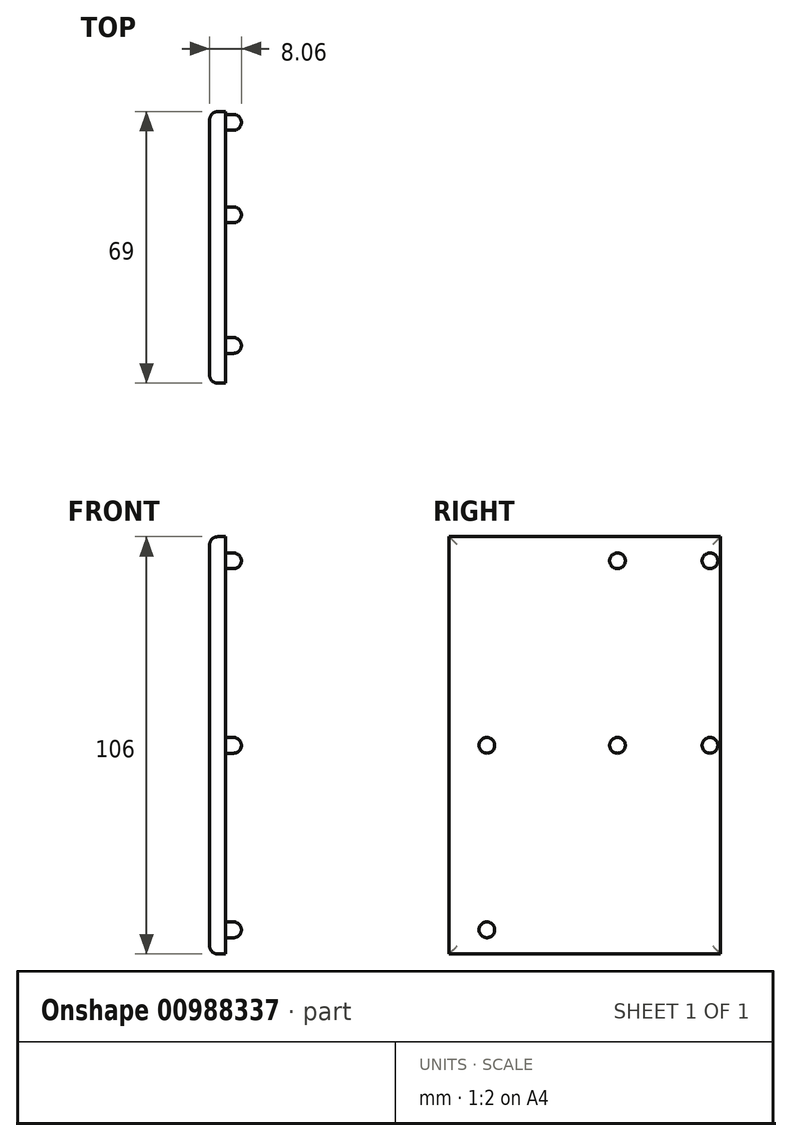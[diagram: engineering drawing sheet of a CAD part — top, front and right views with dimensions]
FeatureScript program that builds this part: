
annotation { "Feature Type Name" : "Feature", "Feature Type Description" : "" }
export const myFeature = defineFeature(function(context is Context, id is Id, definition is map)
    precondition{}
    {
        {
            var Q0;
            Q0=qCreatedBy(makeId("Front.planeOp"),FACE);
            var sketch = newSketch(context, id + "F0", { "sketchPlane" : qUnion([Q0])});
            skLineSegment(sketch, "E0.bottom", {"start": v(70.94, 60) * mm, "end": v(-59.06, 60) * mm});
            skLineSegment(sketch, "E0.top", {"start": v(70.94, -60) * mm, "end": v(-59.06, -60) * mm});
            skLineSegment(sketch, "E0.left", {"start": v(70.94, 60) * mm, "end": v(70.94, -60) * mm});
            skLineSegment(sketch, "E0.right", {"start": v(-59.06, 60) * mm, "end": v(-59.06, -60) * mm});
            skLineSegment(sketch, "E1.bottom", {"start": v(-59.06, 60) * mm, "end": v(70.94, 60) * mm});
            skLineSegment(sketch, "E1.top", {"start": v(-59.06, 53) * mm, "end": v(70.94, 53) * mm});
            skLineSegment(sketch, "E1.left", {"start": v(-59.06, 60) * mm, "end": v(-59.06, 53) * mm});
            skLineSegment(sketch, "E1.right", {"start": v(70.94, 60) * mm, "end": v(70.94, 53) * mm});
            skLineSegment(sketch, "E2.bottom", {"start": v(-59.06, -60) * mm, "end": v(70.94, -60) * mm});
            skLineSegment(sketch, "E2.top", {"start": v(-59.06, -53) * mm, "end": v(70.94, -53) * mm});
            skLineSegment(sketch, "E2.left", {"start": v(-59.06, -60) * mm, "end": v(-59.06, -53) * mm});
            skLineSegment(sketch, "E2.right", {"start": v(70.94, -60) * mm, "end": v(70.94, -53) * mm});
            skLineSegment(sketch, "E3.bottom", {"start": v(-59.06, 53) * mm, "end": v(-52.06, 53) * mm});
            skLineSegment(sketch, "E3.top", {"start": v(-59.06, -53) * mm, "end": v(-52.06, -53) * mm});
            skLineSegment(sketch, "E3.left", {"start": v(-59.06, 53) * mm, "end": v(-59.06, -53) * mm});
            skLineSegment(sketch, "E3.right", {"start": v(-52.06, 53) * mm, "end": v(-52.06, -53) * mm});
            skLineSegment(sketch, "E4.bottom", {"start": v(70.94, 53) * mm, "end": v(64.94, 53) * mm});
            skLineSegment(sketch, "E4.top", {"start": v(70.94, -53) * mm, "end": v(64.94, -53) * mm});
            skLineSegment(sketch, "E4.left", {"start": v(70.94, 53) * mm, "end": v(70.94, -53) * mm});
            skLineSegment(sketch, "E4.right", {"start": v(64.94, 53) * mm, "end": v(64.94, -53) * mm});
            skLineSegment(sketch, "E5", {"start": v(5.94, -53) * mm, "end": v(5.94, -60) * mm});
            skPoint(sketch, "E6", {"position": v(5.94, -55.5) * mm});
            skCircle(sketch, "E7", {"center": v(5.94, -55.5) * mm, "radius": 2.5 * mm});
            skLineSegment(sketch, "E8.MirrorCS", {"start": v(5.94, 53) * mm, "end": v(5.94, 60) * mm});
            skCircle(sketch, "E9.MirrorC", {"center": v(5.94, 55.5) * mm, "radius": 2.5 * mm});
            skLineSegment(sketch, "E10", {"start": v(-59.06, 0) * mm, "end": v(-52.06, 0) * mm});
            skLineSegment(sketch, "E11", {"start": v(64.94, 0) * mm, "end": v(70.94, 0) * mm});
            skPoint(sketch, "E12", {"position": v(-54.56, 0) * mm});
            skPoint(sketch, "E13", {"position": v(67.44, 0) * mm});
            skCircle(sketch, "E14", {"center": v(67.44, 0) * mm, "radius": 2.5 * mm});
            skPoint(sketch, "E15", {"position": v(-52.06, 55.5) * mm});
            skPoint(sketch, "E16", {"position": v(64.94, 55.5) * mm});
            skCircle(sketch, "E17", {"center": v(64.94, 55.5) * mm, "radius": 2.5 * mm});
            skCircle(sketch, "E18.MirrorC", {"center": v(64.94, -55.5) * mm, "radius": 2.5 * mm});
            skPoint(sketch, "E19", {"position": v(-54.56, -47) * mm});
            skPoint(sketch, "E20", {"position": v(67.44, 47) * mm});
            skCircle(sketch, "E21", {"center": v(67.44, 47) * mm, "radius": 2.5 * mm});
            skCircle(sketch, "E22.MirrorC", {"center": v(67.44, -47) * mm, "radius": 2.5 * mm});
            skCircle(sketch, "E23", {"center": v(5.94, -55.5) * mm, "radius": 2.35 * mm});
            skCircle(sketch, "E24", {"center": v(5.94, 55.5) * mm, "radius": 2.35 * mm});
            skCircle(sketch, "E25", {"center": v(64.94, 55.5) * mm, "radius": 2.35 * mm});
            skCircle(sketch, "E26", {"center": v(67.44, 47) * mm, "radius": 2.35 * mm});
            skCircle(sketch, "E27", {"center": v(67.44, 0) * mm, "radius": 2.35 * mm});
            skCircle(sketch, "E28", {"center": v(67.44, -47) * mm, "radius": 2.35 * mm});
            skCircle(sketch, "E29", {"center": v(64.94, -55.5) * mm, "radius": 2.35 * mm});
            skLineSegment(sketch, "E30.bottom", {"start": v(-59.06, 53) * mm, "end": v(-63.06, 53) * mm});
            skLineSegment(sketch, "E30.top", {"start": v(-59.06, -53) * mm, "end": v(-63.06, -53) * mm});
            skLineSegment(sketch, "E30.right", {"start": v(-63.06, 53) * mm, "end": v(-63.06, -53) * mm});
            skSolve(sketch);
        }
        {
            var Q0;
            {var subQ3=sQuery(id+"F0.wireOp",EDGE,"E30.bottom");Q0=makeQuery(id+"F0.imprint","IMPRINT",FACE,{"disambiguationData":[TD([[makeQuery(id+"F0.imprint","IMPRINT",EDGE,{"derivedFrom":subQ3}),1.0]])]});}
            extrude(context, id + "F1", {"entities" : qUnion([Q0]), "depth" : 80 * mm, "offsetDistance" : 25 * mm, "hasSecondDirection" : true, "secondDirectionOppositeDirection" : false, "secondDirectionDepth" : 11 * mm});
        }
        {
            var Q0;
            Q0=qCreatedBy(makeId("Right.planeOp"),FACE);
            cPlane(context, id + "F2", {"entities" : qUnion([Q0]), "cplaneType" : CPlaneType.OFFSET, "offset" : 81 * mm, "oppositeDirection" : true, "width" : 150 * mm, "height" : 150 * mm});
        }
        {
            var Q0;
            Q0=qCreatedBy(id+"F2.planeOp",FACE);
            var sketch = newSketch(context, id + "F3", { "sketchPlane" : qUnion([Q0])});
            skLineSegment(sketch, "E31.bottom", {"start": v(-56.68, 41.82) * mm, "end": v(-41.3, 41.82) * mm});
            skLineSegment(sketch, "E31.top", {"start": v(-56.68, -13.63) * mm, "end": v(-41.3, -13.63) * mm});
            skLineSegment(sketch, "E31.left", {"start": v(-56.68, 41.82) * mm, "end": v(-56.68, -13.63) * mm});
            skLineSegment(sketch, "E31.right", {"start": v(-41.3, 41.82) * mm, "end": v(-41.3, -13.63) * mm});
            skCircle(sketch, "E32", {"center": v(-70.4, 0) * mm, "radius": 2 * mm});
            skCircle(sketch, "E33", {"center": v(-70.4, -46.88) * mm, "radius": 2 * mm});
            skCircle(sketch, "E34.MirrorC", {"center": v(-70.4, 46.88) * mm, "radius": 2 * mm});
            skCircle(sketch, "E35", {"center": v(-37.22, 46.88) * mm, "radius": 2 * mm});
            skCircle(sketch, "E36", {"center": v(-13.73, 46.88) * mm, "radius": 2 * mm});
            skCircle(sketch, "E37.MirrorC", {"center": v(-37.22, -46.88) * mm, "radius": 2 * mm});
            skCircle(sketch, "E38.MirrorC", {"center": v(-13.73, -46.88) * mm, "radius": 2 * mm});
            skCircle(sketch, "E39", {"center": v(-37.22, 0) * mm, "radius": 2 * mm});
            skCircle(sketch, "E40", {"center": v(-13.73, 0) * mm, "radius": 2 * mm});
            skSolve(sketch);
        }
        {
            var Q0;
            Q0=makeQuery(id+"F3.imprint","IMPRINT",FACE,{"disambiguationData":[TD([[makeQuery(id+"F3.imprint","IMPRINT",EDGE,{"derivedFrom":sQuery(id+"F3.wireOp",EDGE,"E33")}),1.0]])]});
            var Q1;
            Q1=makeQuery(id+"F3.imprint","IMPRINT",FACE,{"disambiguationData":[TD([[makeQuery(id+"F3.imprint","IMPRINT",EDGE,{"derivedFrom":sQuery(id+"F3.wireOp",EDGE,"E32")}),1.0]])]});
            var Q2;
            Q2=makeQuery(id+"F3.imprint","IMPRINT",FACE,{"disambiguationData":[TD([[makeQuery(id+"F3.imprint","IMPRINT",EDGE,{"derivedFrom":sQuery(id+"F3.wireOp",EDGE,"E34.MirrorC")}),-1.0]])]});
            var Q3;
            Q3=makeQuery(id+"F3.imprint","IMPRINT",FACE,{"disambiguationData":[TD([[makeQuery(id+"F3.imprint","IMPRINT",EDGE,{"derivedFrom":sQuery(id+"F3.wireOp",EDGE,"E35")}),1.0]])]});
            var Q4;
            Q4=makeQuery(id+"F3.imprint","IMPRINT",FACE,{"disambiguationData":[TD([[makeQuery(id+"F3.imprint","IMPRINT",EDGE,{"derivedFrom":sQuery(id+"F3.wireOp",EDGE,"E39")}),1.0]])]});
            var Q5;
            Q5=makeQuery(id+"F3.imprint","IMPRINT",FACE,{"disambiguationData":[TD([[makeQuery(id+"F3.imprint","IMPRINT",EDGE,{"derivedFrom":sQuery(id+"F3.wireOp",EDGE,"E37.MirrorC")}),-1.0]])]});
            var Q6;
            Q6=makeQuery(id+"F3.imprint","IMPRINT",FACE,{"disambiguationData":[TD([[makeQuery(id+"F3.imprint","IMPRINT",EDGE,{"derivedFrom":sQuery(id+"F3.wireOp",EDGE,"E36")}),1.0]])]});
            var Q7;
            Q7=makeQuery(id+"F3.imprint","IMPRINT",FACE,{"disambiguationData":[TD([[makeQuery(id+"F3.imprint","IMPRINT",EDGE,{"derivedFrom":sQuery(id+"F3.wireOp",EDGE,"E40")}),1.0]])]});
            var Q8;
            Q8=makeQuery(id+"F3.imprint","IMPRINT",FACE,{"disambiguationData":[TD([[makeQuery(id+"F3.imprint","IMPRINT",EDGE,{"derivedFrom":sQuery(id+"F3.wireOp",EDGE,"E38.MirrorC")}),-1.0]])]});
            extrude(context, id + "F4", {"entities" : qUnion([Q0, Q1, Q2, Q3, Q4, Q5, Q6, Q7, Q8]), "operationType" : NewBodyOperationType.ADD, "depth" : 26 * mm, "offsetDistance" : 25 * mm, "hasSecondDirection" : true, "secondDirectionOppositeDirection" : false, "secondDirectionDepth" : 21.75 * mm});
        }
        {
            var Q0;
            Q0=makeQuery(id+"F4.opExtrude","CAP_FACE",FACE,{"disambiguationData":[OSD([sQuery(id+"F3.wireOp",EDGE,"E32")])],"isStart":false});
            var Q1;
            Q1=makeQuery(id+"F4.opExtrude","CAP_FACE",FACE,{"disambiguationData":[OSD([sQuery(id+"F3.wireOp",EDGE,"E34.MirrorC")])],"isStart":false});
            var Q2;
            Q2=makeQuery(id+"F4.opExtrude","CAP_FACE",FACE,{"disambiguationData":[OSD([sQuery(id+"F3.wireOp",EDGE,"E33")])],"isStart":false});
            var Q3;
            Q3=makeQuery(id+"F4.opExtrude","CAP_FACE",FACE,{"disambiguationData":[OSD([sQuery(id+"F3.wireOp",EDGE,"E37.MirrorC")])],"isStart":false});
            var Q4;
            Q4=makeQuery(id+"F4.opExtrude","CAP_FACE",FACE,{"disambiguationData":[OSD([sQuery(id+"F3.wireOp",EDGE,"E39")])],"isStart":false});
            var Q5;
            Q5=makeQuery(id+"F4.opExtrude","CAP_EDGE",EDGE,{"disambiguationData":[OSD([sQuery(id+"F3.wireOp",EDGE,"E35")])],"isStart":false});
            var Q6;
            Q6=makeQuery(id+"F4.opExtrude","CAP_EDGE",EDGE,{"disambiguationData":[OSD([sQuery(id+"F3.wireOp",EDGE,"E36")])],"isStart":false});
            var Q7;
            Q7=makeQuery(id+"F4.opExtrude","CAP_EDGE",EDGE,{"disambiguationData":[OSD([sQuery(id+"F3.wireOp",EDGE,"E40")])],"isStart":false});
            var Q8;
            Q8=makeQuery(id+"F4.opExtrude","CAP_EDGE",EDGE,{"disambiguationData":[OSD([sQuery(id+"F3.wireOp",EDGE,"E38.MirrorC")])],"isStart":false});
            fillet(context, id + "F5", {"entities" : qUnion([Q0, Q1, Q2, Q3, Q4, Q5, Q6, Q7, Q8]), "tangentPropagation" : true, "radius" : 2 * mm, "defaultsChanged" : true, "vertexSettings" : [], "allowEdgeOverflow" : false});
        }
        {
            var Q0;
            Q0=makeQuery(id+"F1.opExtrude","SWEPT_FACE",FACE,{"disambiguationData":[OSD([sQuery(id+"F0.wireOp",EDGE,"E30.right")])]});
            fillet(context, id + "F6", {"entities" : qUnion([Q0]), "tangentPropagation" : true, "radius" : 2 * mm, "defaultsChanged" : true, "vertexSettings" : [], "allowEdgeOverflow" : false});
        }
    });
